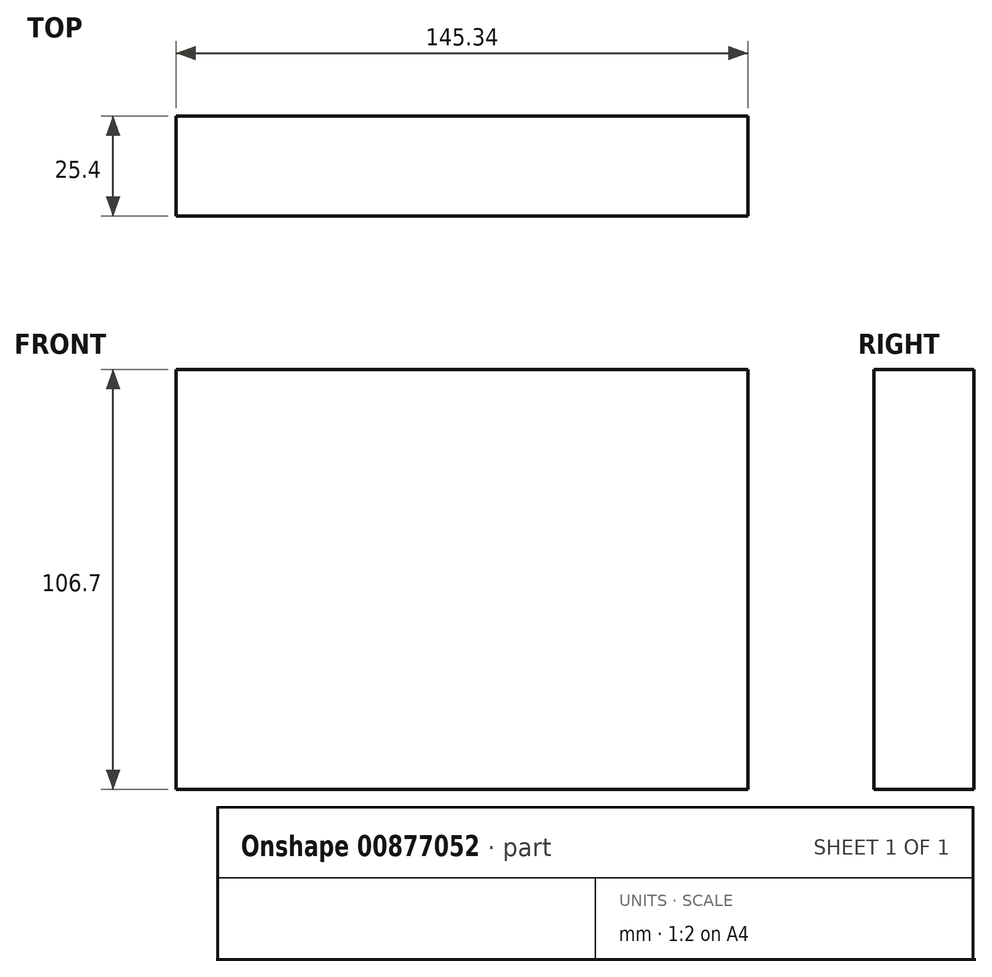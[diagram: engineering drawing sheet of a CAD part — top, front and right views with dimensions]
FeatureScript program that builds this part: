
annotation { "Feature Type Name" : "Feature", "Feature Type Description" : "" }
export const myFeature = defineFeature(function(context is Context, id is Id, definition is map)
    precondition{}
    {
        {
            var Q0;
            Q0=qCreatedBy(makeId("Front.planeOp"),FACE);
            var sketch = newSketch(context, id + "F0", { "sketchPlane" : qUnion([Q0])});
            skLineSegment(sketch, "E0.bottom", {"start": v(0, 0) * mm, "end": v(0, 0) * mm});
            skLineSegment(sketch, "E0.top", {"start": v(0, 0) * mm, "end": v(0, 0) * mm});
            skLineSegment(sketch, "E0.left", {"start": v(0, 0) * mm, "end": v(0, 0) * mm});
            skLineSegment(sketch, "E0.right", {"start": v(0, 0) * mm, "end": v(0, 0) * mm});
            skPoint(sketch, "E0.middle", {"position": v(0, 0) * mm});
            skLineSegment(sketch, "E1.bottom", {"start": v(72.67, 53.35) * mm, "end": v(-72.67, 53.35) * mm});
            skLineSegment(sketch, "E1.top", {"start": v(72.67, -53.35) * mm, "end": v(-72.67, -53.35) * mm});
            skLineSegment(sketch, "E1.left", {"start": v(72.67, 53.35) * mm, "end": v(72.67, -53.35) * mm});
            skLineSegment(sketch, "E1.right", {"start": v(-72.67, 53.35) * mm, "end": v(-72.67, -53.35) * mm});
            skSolve(sketch);
        }
        {
            var Q0;
            Q0=makeQuery(id+"F0.imprint","IMPRINT",FACE,{"disambiguationData":[TD([[makeQuery(id+"F0.imprint","IMPRINT",EDGE,{"derivedFrom":sQuery(id+"F0.wireOp",EDGE,"E1.bottom")}),1.0]])]});
            extrude(context, id + "F1", {"entities" : qUnion([Q0]), "depth" : 25.4 * mm, "offsetDistance" : 25.4 * mm});
        }
        {
            var Q0;
            Q0=makeQuery(id+"F1.opExtrude","CAP_FACE",FACE,{"disambiguationData":[OSD([sQuery(id+"F0.wireOp",EDGE,"E1.bottom"),sQuery(id+"F0.wireOp",EDGE,"E1.top"),sQuery(id+"F0.wireOp",EDGE,"E1.left"),sQuery(id+"F0.wireOp",EDGE,"E1.right")])],"isStart":false});
            var sketch = newSketch(context, id + "F2", { "sketchPlane" : qUnion([Q0])});
            skCircle(sketch, "E2", {"center": v(0, 0) * mm, "radius": 41.12 * mm});
            skSolve(sketch);
        }
        {
            var Q0;
            Q0=sQuery(id+"F2.wireOp",EDGE,"E2");
            extrude(context, id + "F3", {"bodyType" : ToolBodyType.SURFACE, "surfaceEntities" : qUnion([Q0]), "endBound" : BoundingType.SYMMETRIC, "depth" : 50 * mm, "offsetDistance" : 25.4 * mm});
        }
    });
